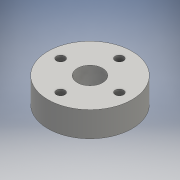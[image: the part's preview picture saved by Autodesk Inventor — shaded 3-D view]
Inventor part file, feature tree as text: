
AUTODESK INVENTOR PART (.ipt)
format: ipt  version: 2016 (Build 200138000, 138)  size: 124,928 bytes
history: native  units: mm
features: extrude x2, sketch x2, other x1
ambient origin geometry x8: Origin, YZ Plane, XZ Plane, XY Plane, X Axis, Y Axis, Z Axis, Center Point
bodies: Body1 (feature_tree)
feature tree (5):
  other  "ソリッド1"
  extrude  "押し出し1"  Depth=6.0mm
  extrude  "押し出し3"  Depth=20.0mm
  sketch  "スケッチ1"
  sketch  "スケッチ3"
